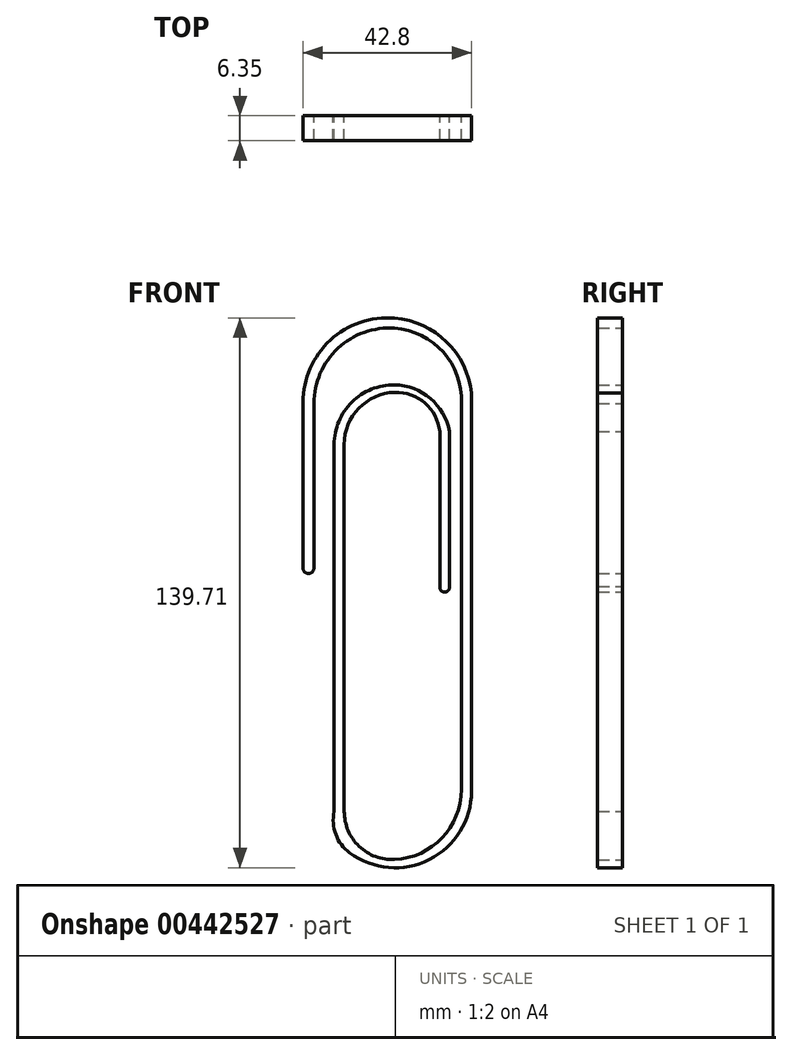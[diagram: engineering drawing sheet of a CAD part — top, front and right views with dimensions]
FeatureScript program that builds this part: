
annotation { "Feature Type Name" : "Feature", "Feature Type Description" : "" }
export const myFeature = defineFeature(function(context is Context, id is Id, definition is map)
    precondition{}
    {
        {
            var Q0;
            Q0=qCreatedBy(makeId("Front.planeOp"),FACE);
            var sketch = newSketch(context, id + "F0", { "sketchPlane" : qUnion([Q0])});
            skLineSegment(sketch, "E0", {"start": v(-23.26, 0) * mm, "end": v(-23.26, 42.1) * mm});
            skArc(sketch, "E1", {"start": v(-23.26, 42.1) * mm, "mid": v(-16.32, 57.9) * mm, "end": v(0, 63.5) * mm});
            skArc(sketch, "E2", {"start": v(0, 63.5) * mm, "mid": v(13.2, 57.47) * mm, "end": v(19.54, 44.42) * mm});
            skLineSegment(sketch, "E3", {"start": v(19.54, 44.42) * mm, "end": v(19.54, -56.75) * mm});
            skArc(sketch, "E4", {"start": v(19.54, -56.75) * mm, "mid": v(8.87, -74.07) * mm, "end": v(-11.4, -72.33) * mm});
            skArc(sketch, "E5", {"start": v(-11.4, -72.33) * mm, "mid": v(-14.91, -67.68) * mm, "end": v(-15.35, -61.87) * mm});
            skLineSegment(sketch, "E6", {"start": v(-15.35, -61.87) * mm, "end": v(-15.35, 31.4) * mm});
            skArc(sketch, "E7", {"start": v(-15.35, 31.4) * mm, "mid": v(-10.84, 42.17) * mm, "end": v(0, 46.52) * mm});
            skArc(sketch, "E8", {"start": v(0, 46.52) * mm, "mid": v(9.1, 43.1) * mm, "end": v(13.96, 34.66) * mm});
            skLineSegment(sketch, "E9", {"start": v(-23.26, 0) * mm, "end": v(-20.47, 0) * mm});
            skLineSegment(sketch, "E10", {"start": v(-20.47, 0) * mm, "end": v(-20.47, 41.87) * mm});
            skArc(sketch, "E11", {"start": v(-20.47, 41.87) * mm, "mid": v(-14.38, 55.85) * mm, "end": v(0, 60.94) * mm});
            skArc(sketch, "E12", {"start": v(0, 60.94) * mm, "mid": v(12.37, 54.86) * mm, "end": v(16.98, 41.87) * mm});
            skLineSegment(sketch, "E13", {"start": v(16.98, 41.87) * mm, "end": v(16.98, -56.29) * mm});
            skArc(sketch, "E14", {"start": v(16.98, -56.29) * mm, "mid": v(12.05, -68.58) * mm, "end": v(0, -74.07) * mm});
            skPoint(sketch, "E14.endSnap0", {"position": v(8.87, -74.07) * mm});
            skArc(sketch, "E15", {"start": v(0, -74.07) * mm, "mid": v(-9, -70.7) * mm, "end": v(-12.8, -61.87) * mm});
            skLineSegment(sketch, "E16", {"start": v(-12.8, -61.87) * mm, "end": v(-12.8, 31.4) * mm});
            skArc(sketch, "E17", {"start": v(-12.8, 31.4) * mm, "mid": v(-9.07, 40.61) * mm, "end": v(0, 44.66) * mm});
            skLineSegment(sketch, "E18", {"start": v(13.96, 34.66) * mm, "end": v(13.96, -4.64) * mm});
            skArc(sketch, "E19", {"start": v(0, 44.66) * mm, "mid": v(7.71, 41.92) * mm, "end": v(11.48, 34.66) * mm});
            skLineSegment(sketch, "E20", {"start": v(11.48, 34.66) * mm, "end": v(11.48, -4.87) * mm});
            skArc(sketch, "E21", {"start": v(11.48, -4.87) * mm, "mid": v(12.84, -6.1) * mm, "end": v(13.96, -4.64) * mm});
            skArc(sketch, "E22", {"start": v(-23.26, 0) * mm, "mid": v(-21.86, -1.4) * mm, "end": v(-20.47, 0) * mm});
            skSolve(sketch);
        }
        {
            var Q0;
            Q0=makeQuery(id+"F0.imprint","IMPRINT",FACE,{"disambiguationData":[TD([[makeQuery(id+"F0.imprint","IMPRINT",EDGE,{"derivedFrom":sQuery(id+"F0.wireOp",EDGE,"E0")}),-1.0]])]});
            var Q1;
            Q1=makeQuery(id+"F0.imprint","IMPRINT",FACE,{"disambiguationData":[TD([[makeQuery(id+"F0.imprint","IMPRINT",EDGE,{"derivedFrom":sQuery(id+"F0.wireOp",EDGE,"E9")}),-1.0]])]});
            extrude(context, id + "F1", {"entities" : qUnion([Q0, Q1]), "depth" : 6.35 * mm});
        }
    });
